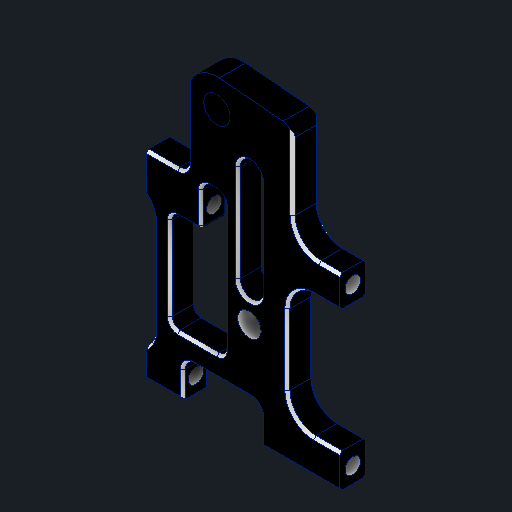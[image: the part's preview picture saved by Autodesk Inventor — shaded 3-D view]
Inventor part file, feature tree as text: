
AUTODESK INVENTOR PART (.ipt)
format: ipt  version: 2025 (Build 290162010, 162A)  size: 338,944 bytes
history: native  units: mm
features: extrude x4, thread x4, projected_geometry x3, chamfer x2, sketch x1
ambient origin geometry x8: Origin, YZ Plane, XZ Plane, XY Plane, X Axis, Y Axis, Z Axis, Center Point
bodies: Solid1 (feature_tree)
feature tree (14):
  extrude  "Extrusion1"  Depth=0.5mm TaperAngle=45.0deg
  chamfer  "Chamfer1"  Distance=0.5mm Angle=45.0deg
  chamfer  "Chamfer2"  Distance=3.0mm
  extrude  "Extrusion2"  Depth=30.0mm
  extrude  "Extrusion3"  Depth=4.5mm
  thread  "Thread1"  [1 undecoded]
  thread  "Thread2"  [1 undecoded]
  thread  "Thread3"  [1 undecoded]
  thread  "Thread4"  [1 undecoded]
  extrude  "Extrusion4"  Depth=7.0mm TaperAngle=0.0deg
  sketch  "Sketch1"  dims[d0=5.0mm d1=0.0mm d2=0.5mm d3=2.0mm d4=45.0deg d5=0.5mm d6=2.0mm d7=45.0deg d8=3.0mm d9=30.0mm d10=3.0mm d11=3.0mm d12=0.0mm d13=10.0mm d14=0.0mm d15=10.5mm d16=0.0mm d17=7.0mm d18=0.0mm d19=15.0mm d20=0.0mm d21=15.0mm d22=0.0mm d23=4.5mm d24=0.0mm d25=0.0mm]
  projected_geometry  "Projected Loop1"
  projected_geometry  "Projected Loop2"
  projected_geometry  "Projected Loop3"
note: 4 required parameter values undecoded (feature->parameter linkage not recoverable at this tier; creation-order binding heuristic only, values carry confidence <= 0.55)
